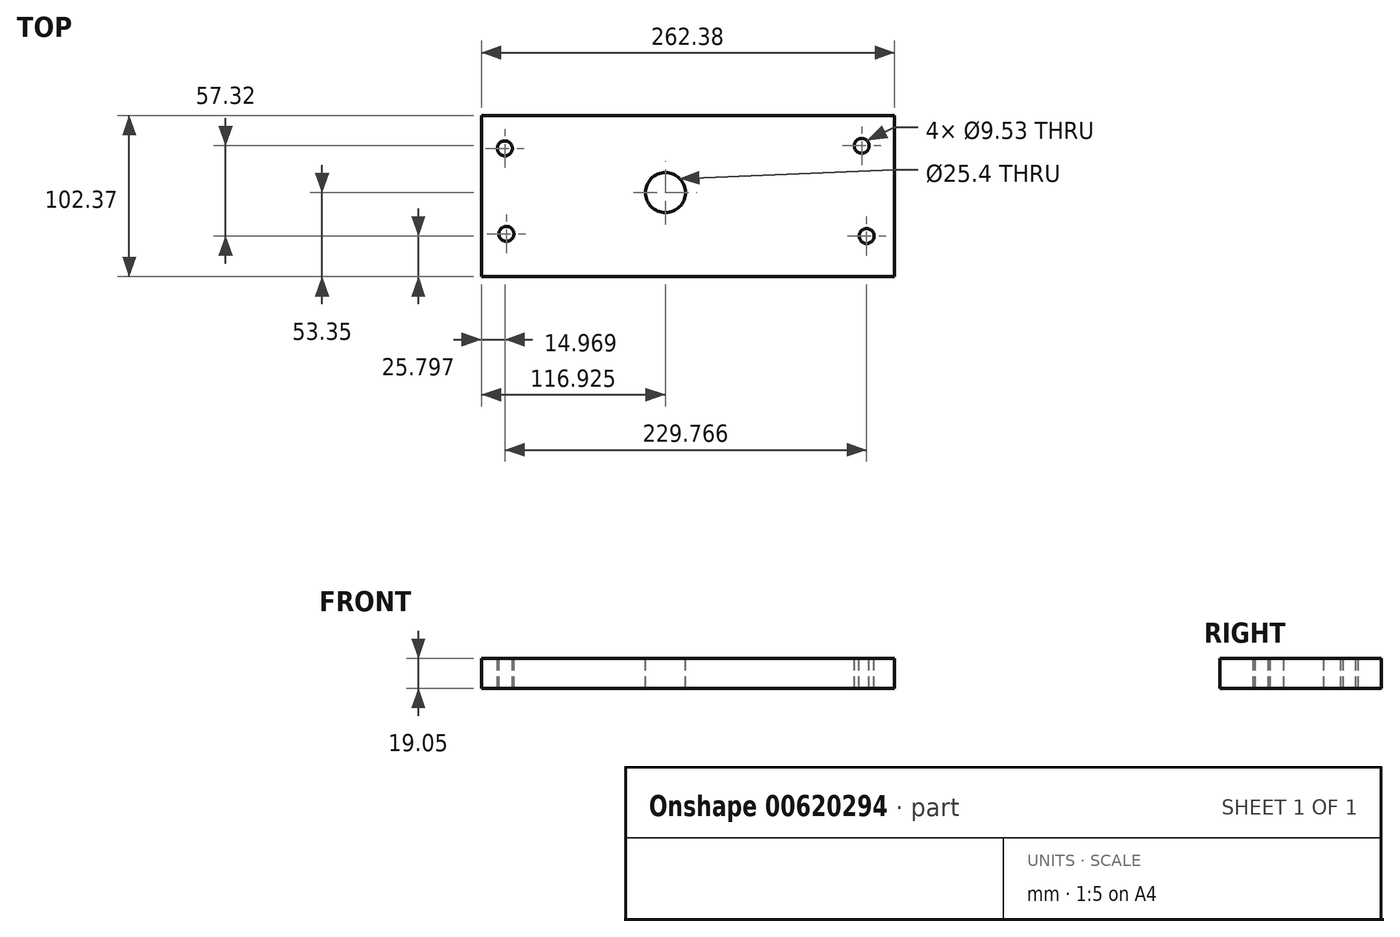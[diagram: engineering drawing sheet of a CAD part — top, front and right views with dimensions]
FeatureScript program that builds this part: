
annotation { "Feature Type Name" : "Feature", "Feature Type Description" : "" }
export const myFeature = defineFeature(function(context is Context, id is Id, definition is map)
    precondition{}
    {
        {
            var Q0;
            Q0=qCreatedBy(makeId("Top.planeOp"),FACE);
            var sketch = newSketch(context, id + "F0", { "sketchPlane" : qUnion([Q0])});
            skLineSegment(sketch, "E0.bottom", {"start": v(0, 0) * mm, "end": v(262.38, 0) * mm});
            skLineSegment(sketch, "E0.top", {"start": v(0, 102.37) * mm, "end": v(262.38, 102.37) * mm});
            skLineSegment(sketch, "E0.left", {"start": v(0, 0) * mm, "end": v(0, 102.37) * mm});
            skLineSegment(sketch, "E0.right", {"start": v(262.38, 0) * mm, "end": v(262.38, 102.37) * mm});
            skSolve(sketch);
        }
        {
            var Q0;
            Q0=makeQuery(id+"F0.imprint","IMPRINT",FACE,{"disambiguationData":[TD([[makeQuery(id+"F0.imprint","IMPRINT",EDGE,{"derivedFrom":sQuery(id+"F0.wireOp",EDGE,"E0.bottom")}),1.0]])]});
            extrude(context, id + "F1", {"entities" : qUnion([Q0]), "depth" : 19.05 * mm, "offsetDistance" : 25.4 * mm});
        }
        {
            var Q0;
            Q0=makeQuery(id+"F1.opExtrude","CAP_FACE",FACE,{"disambiguationData":[OSD([sQuery(id+"F0.wireOp",EDGE,"E0.bottom"),sQuery(id+"F0.wireOp",EDGE,"E0.top"),sQuery(id+"F0.wireOp",EDGE,"E0.left"),sQuery(id+"F0.wireOp",EDGE,"E0.right")])],"isStart":false});
            var sketch = newSketch(context, id + "F2", { "sketchPlane" : qUnion([Q0])});
            skPoint(sketch, "E1", {"position": v(116.93, 53.35) * mm});
            skSolve(sketch);
        }
        {
            var Q0;
            Q0=sQuery(id+"F2.wireOp",VERTEX,"E1");
            var Q1;
            Q1=makeQuery(id+"F1.opExtrude","SWEPT_BODY",BODY,{"disambiguationData":[OSD([sQuery(id+"F0.wireOp",EDGE,"E0.bottom"),sQuery(id+"F0.wireOp",EDGE,"E0.top"),sQuery(id+"F0.wireOp",EDGE,"E0.left"),sQuery(id+"F0.wireOp",EDGE,"E0.right")])]});
            hole(context, id + "F3", {"style" : HoleStyle.SIMPLE, "endStyle" : HoleEndStyle.THROUGH, "holeDiameter" : 25.4 * mm, "majorDiameter" : 6.35 * mm, "isTappedThrough" : true, "tappedDepth" : 12.7 * mm, "tapClearance" : 3, "locations" : qUnion([Q0]), "scope" : qUnion([Q1])});
        }
        {
            var Q0;
            Q0=makeQuery(id+"F1.opExtrude","CAP_FACE",FACE,{"disambiguationData":[OSD([sQuery(id+"F0.wireOp",EDGE,"E0.bottom"),sQuery(id+"F0.wireOp",EDGE,"E0.top"),sQuery(id+"F0.wireOp",EDGE,"E0.left"),sQuery(id+"F0.wireOp",EDGE,"E0.right")])],"isStart":false});
            var sketch = newSketch(context, id + "F4", { "sketchPlane" : qUnion([Q0])});
            skPoint(sketch, "E2", {"position": v(14.97, 81.47) * mm});
            skPoint(sketch, "E3", {"position": v(15.94, 27.14) * mm});
            skPoint(sketch, "E4", {"position": v(241.62, 83.12) * mm});
            skPoint(sketch, "E5", {"position": v(244.73, 25.8) * mm});
            skSolve(sketch);
        }
        {
            var Q0;
            Q0=sQuery(id+"F4.wireOp",VERTEX,"E2");
            var Q1;
            Q1=sQuery(id+"F4.wireOp",VERTEX,"E3");
            var Q2;
            Q2=sQuery(id+"F4.wireOp",VERTEX,"E4");
            var Q3;
            Q3=sQuery(id+"F4.wireOp",VERTEX,"E5");
            var Q4;
            Q4=makeQuery(id+"F1.opExtrude","SWEPT_BODY",BODY,{"disambiguationData":[OSD([sQuery(id+"F0.wireOp",EDGE,"E0.bottom"),sQuery(id+"F0.wireOp",EDGE,"E0.top"),sQuery(id+"F0.wireOp",EDGE,"E0.left"),sQuery(id+"F0.wireOp",EDGE,"E0.right")])]});
            hole(context, id + "F5", {"style" : HoleStyle.SIMPLE, "endStyle" : HoleEndStyle.THROUGH, "holeDiameter" : 9.52 * mm, "majorDiameter" : 6.35 * mm, "isTappedThrough" : true, "tappedDepth" : 12.7 * mm, "tapClearance" : 3, "locations" : qUnion([Q0, Q1, Q2, Q3]), "scope" : qUnion([Q4])});
        }
    });
